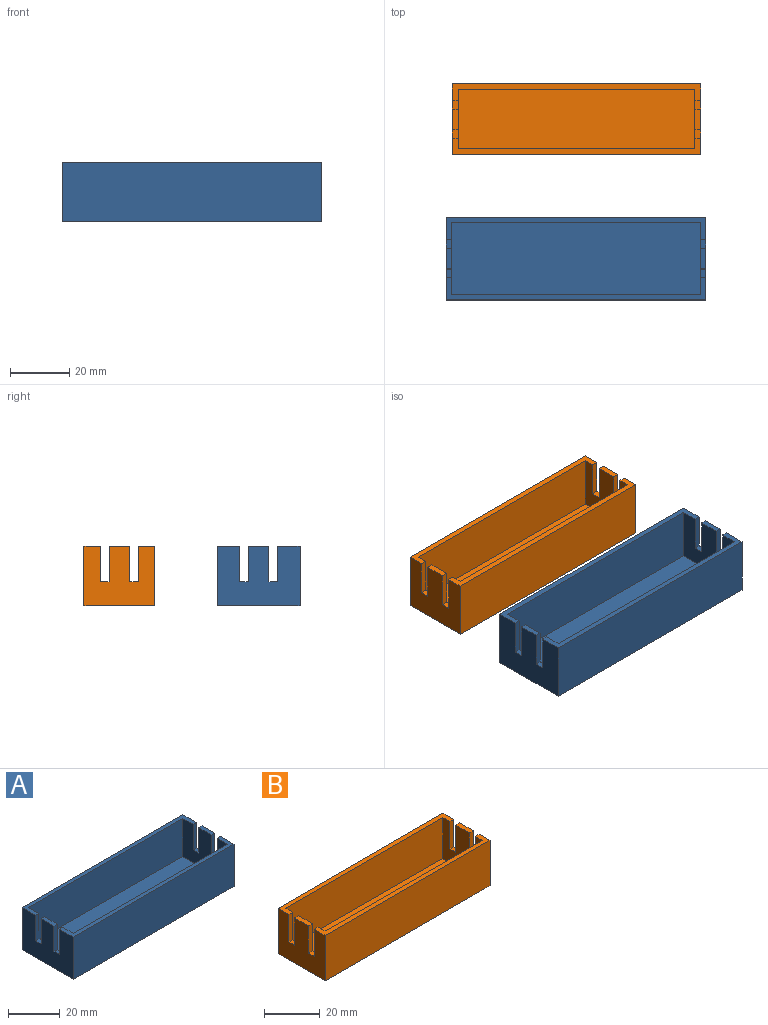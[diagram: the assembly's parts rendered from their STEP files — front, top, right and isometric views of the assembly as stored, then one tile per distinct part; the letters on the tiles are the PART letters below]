
ASSEMBLY  parts=2 mates=1
PART A: 26 faces, bbox 88x28x20 mm
  f0: plane 28x20mm, normal (-1,0,0), area 488mm2, adj f4,f5,f7,f8,f9,f12,f20,f21
  f1: plane 28x20mm, normal (1,0,0), area 488mm2, adj f4,f6,f7,f8,f9,f12,f14,f15
  f2: plane 24.4x18mm, normal (1,0,0), area 367.2mm2, adj f4,f5,f10,f11,f12,f13,f20,f21
  f3: plane 24.4x18mm, normal (-1,0,0), area 367.2mm2, adj f4,f6,f10,f11,f12,f13,f14,f15
  f4: plane 88x7.5mm, normal (0,0,1), area 178.9mm2, adj f0,f1,f2,f3,f7,f10,f17,f24
  f5: plane 7x1.8mm, normal (0,0,1), area 12.6mm2, adj f0,f2,f20,f25
  f6: plane 7x1.8mm, normal (0,0,1), area 12.6mm2, adj f1,f3,f16,f18
  f7: plane 88x20mm, normal (0,1,0), area 1760mm2, adj f0,f1,f4,f9
  f8: plane 88x20mm, normal (0,-1,0), area 1760mm2, adj f0,f1,f9,f12
  f9: plane 88x28mm, normal (0,0,-1), area 2464mm2, adj f0,f1,f7,f8
  f10: plane 84.4x18mm, normal (0,-1,0), area 1519.2mm2, adj f2,f3,f4,f13
  f11: plane 84.4x18mm, normal (0,1,0), area 1519.2mm2, adj f2,f3,f12,f13
  f12: plane 88x7.5mm, normal (0,0,1), area 178.9mm2, adj f0,f1,f2,f3,f8,f11,f15,f21
  f13: plane 84.4x24.4mm, normal (0,0,1), area 2059.4mm2, adj f2,f3,f10,f11
  f14: plane 3x1.8mm, normal (0,0,1), area 5.4mm2, adj f1,f3,f15,f16
  f15: plane 12x1.8mm, normal (0,1,0), area 21.6mm2, adj f1,f3,f12,f14
  f16: plane 12x1.8mm, normal (0,-1,0), area 21.6mm2, adj f1,f3,f6,f14
  f17: plane 12x1.8mm, normal (0,-1,0), area 21.6mm2, adj f1,f3,f4,f19
  f18: plane 12x1.8mm, normal (0,1,0), area 21.6mm2, adj f1,f3,f6,f19
  f19: plane 3x1.8mm, normal (0,0,1), area 5.4mm2, adj f1,f3,f17,f18
  f20: plane 12x1.8mm, normal (0,-1,0), area 21.6mm2, adj f0,f2,f5,f22
  f21: plane 12x1.8mm, normal (0,1,0), area 21.6mm2, adj f0,f2,f12,f22
  f22: plane 3x1.8mm, normal (0,0,1), area 5.4mm2, adj f0,f2,f20,f21
  f23: plane 3x1.8mm, normal (0,0,1), area 5.4mm2, adj f0,f2,f24,f25
  f24: plane 12x1.8mm, normal (0,-1,0), area 21.6mm2, adj f0,f2,f4,f23
  f25: plane 12x1.8mm, normal (0,1,0), area 21.6mm2, adj f0,f2,f5,f23
PART B: 26 faces, bbox 84x24x20 mm
  f0: plane 24x20mm, normal (-1,0,0), area 408mm2, adj f4,f5,f7,f8,f9,f12,f20,f21
  f1: plane 24x20mm, normal (1,0,0), area 408mm2, adj f4,f6,f7,f8,f9,f12,f14,f15
  f2: plane 20x18mm, normal (1,0,0), area 288mm2, adj f4,f5,f10,f11,f12,f13,f20,f21
  f3: plane 20x18mm, normal (-1,0,0), area 288mm2, adj f4,f6,f10,f11,f12,f13,f14,f15
  f4: plane 84x5.5mm, normal (0,0,1), area 182mm2, adj f0,f1,f2,f3,f8,f10,f17,f24
  f5: plane 7x2mm, normal (0,0,1), area 14mm2, adj f0,f2,f22,f25
  f6: plane 7x2mm, normal (0,0,1), area 14mm2, adj f1,f3,f14,f18
  f7: plane 84x20mm, normal (0,-1,0), area 1680mm2, adj f0,f1,f9,f12
  f8: plane 84x20mm, normal (0,1,0), area 1680mm2, adj f0,f1,f4,f9
  f9: plane 84x24mm, normal (0,0,-1), area 2016mm2, adj f0,f1,f7,f8
  f10: plane 80x18mm, normal (0,-1,0), area 1440mm2, adj f2,f3,f4,f13
  f11: plane 80x18mm, normal (0,1,0), area 1440mm2, adj f2,f3,f12,f13
  f12: plane 84x5.5mm, normal (0,0,1), area 182mm2, adj f0,f1,f2,f3,f7,f11,f16,f20
  f13: plane 80x20mm, normal (0,0,1), area 1600mm2, adj f2,f3,f10,f11
  f14: plane 12x2mm, normal (0,-1,0), area 24mm2, adj f1,f3,f6,f15
  f15: plane 3x2mm, normal (0,0,1), area 6mm2, adj f1,f3,f14,f16
  f16: plane 12x2mm, normal (0,1,0), area 24mm2, adj f1,f3,f12,f15
  f17: plane 12x2mm, normal (0,-1,0), area 24mm2, adj f1,f3,f4,f19
  f18: plane 12x2mm, normal (0,1,0), area 24mm2, adj f1,f3,f6,f19
  f19: plane 3x2mm, normal (0,0,1), area 6mm2, adj f1,f3,f17,f18
  f20: plane 12x2mm, normal (0,1,0), area 24mm2, adj f0,f2,f12,f21
  f21: plane 3x2mm, normal (0,0,1), area 6mm2, adj f0,f2,f20,f22
  f22: plane 12x2mm, normal (0,-1,0), area 24mm2, adj f0,f2,f5,f21
  f23: plane 3x2mm, normal (0,0,1), area 6mm2, adj f0,f2,f24,f25
  f24: plane 12x2mm, normal (0,-1,0), area 24mm2, adj f0,f2,f4,f23
  f25: plane 12x2mm, normal (0,1,0), area 24mm2, adj f0,f2,f5,f23
PLACE A t=(-0.19,-23.63,-59.09)mm
PLACE B t=(0,23.5,-9.09)mm
MATE planar B.f9 <-> A.f9  axis (0,0,-1) through (0,23.5,-36.09)mm
